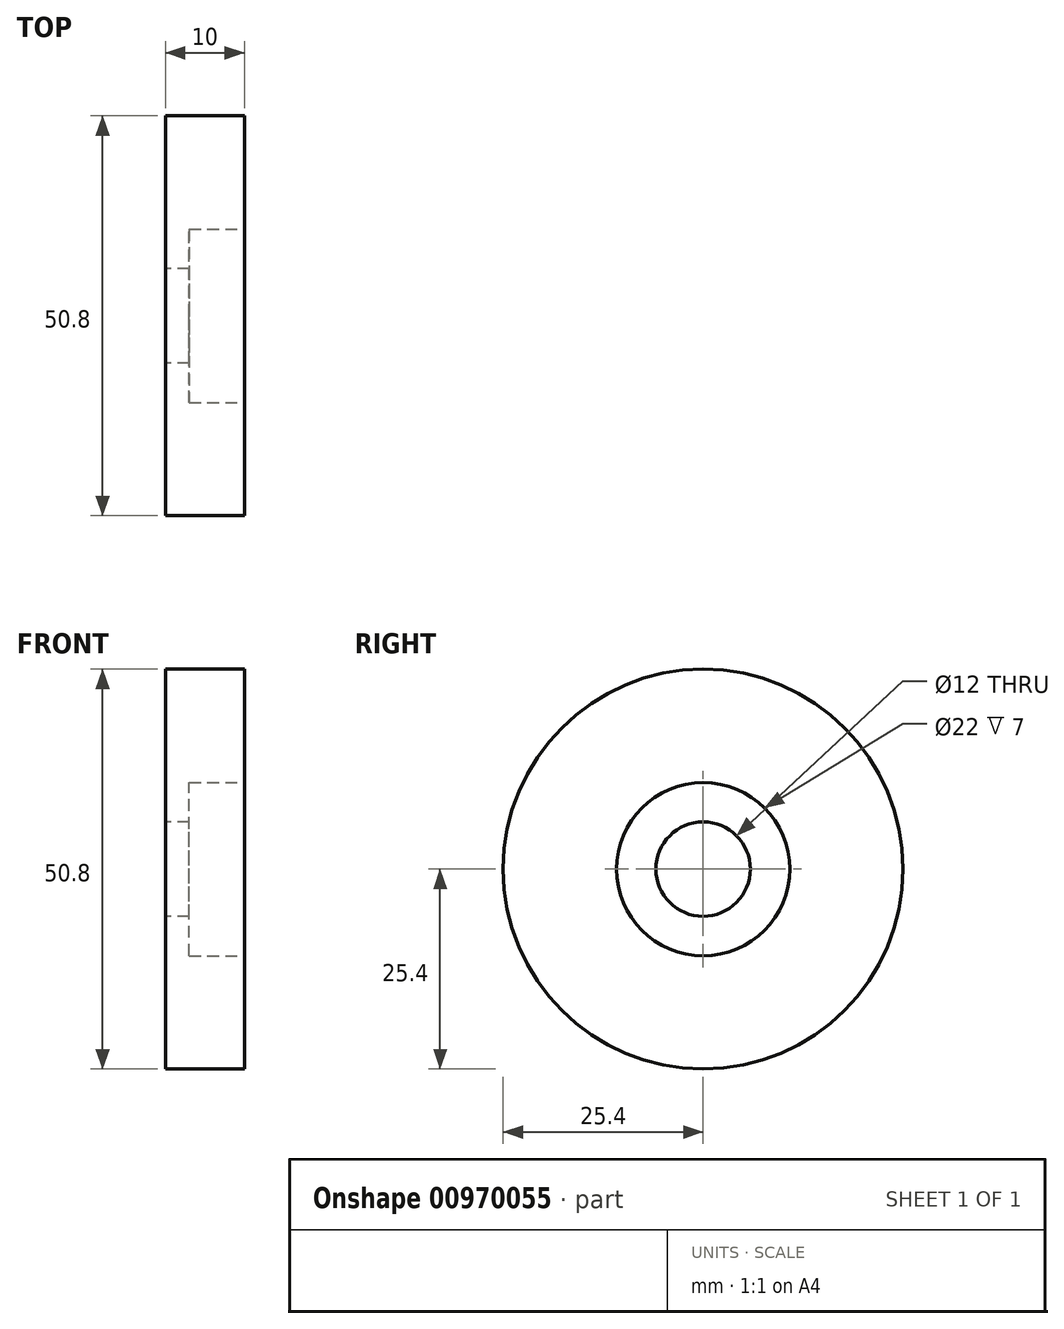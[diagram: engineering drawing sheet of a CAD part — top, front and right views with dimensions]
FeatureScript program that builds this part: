
annotation { "Feature Type Name" : "Feature", "Feature Type Description" : "" }
export const myFeature = defineFeature(function(context is Context, id is Id, definition is map)
    precondition{}
    {
        {
            var Q0;
            Q0=qCreatedBy(makeId("Right.planeOp"),FACE);
            var sketch = newSketch(context, id + "F0", { "sketchPlane" : qUnion([Q0])});
            skCircle(sketch, "E0", {"center": v(0, 0) * mm, "radius": 25.4 * mm});
            skCircle(sketch, "E1", {"center": v(0, 0) * mm, "radius": 6 * mm});
            skSolve(sketch);
        }
        {
            var Q0;
            Q0=makeQuery(id+"F0.imprint","IMPRINT",FACE,{"disambiguationData":[TD([[makeQuery(id+"F0.imprint","IMPRINT",EDGE,{"derivedFrom":sQuery(id+"F0.wireOp",EDGE,"E0")}),1.0]])]});
            extrude(context, id + "F1", {"entities" : qUnion([Q0]), "depth" : 10 * mm, "offsetDistance" : 25.4 * mm});
        }
        {
            var Q0;
            Q0=makeQuery(id+"F1.opExtrude","CAP_FACE",FACE,{"disambiguationData":[OSD([sQuery(id+"F0.wireOp",EDGE,"E0"),sQuery(id+"F0.wireOp",EDGE,"E1")])],"isStart":false});
            var sketch = newSketch(context, id + "F2", { "sketchPlane" : qUnion([Q0])});
            skCircle(sketch, "E2", {"center": v(0, 0) * mm, "radius": 11 * mm});
            skSolve(sketch);
        }
        {
            var Q0;
            Q0=makeQuery(id+"F2.imprint","IMPRINT",FACE,{"disambiguationData":[TD([[makeQuery(id+"F2.imprint","IMPRINT",EDGE,{"derivedFrom":sQuery(id+"F2.wireOp",EDGE,"E2")}),1.0]])]});
            extrude(context, id + "F3", {"entities" : qUnion([Q0]), "operationType" : NewBodyOperationType.REMOVE, "oppositeDirection" : true, "depth" : 7 * mm, "offsetDistance" : 25.4 * mm});
        }
    });
